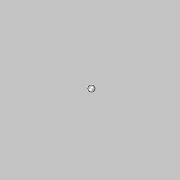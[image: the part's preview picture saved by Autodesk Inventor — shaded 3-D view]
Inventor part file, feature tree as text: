
AUTODESK INVENTOR PART (.ipt)
format: ipt  version: 2017 (Build 210142000, 142)  size: 128,000 bytes
history: native  units: mm
features: other x7, extrude x7, sketch x6, fillet x3, projected_geometry x2, plane x1
ambient origin geometry x7: Origin, YZ Plane, XZ Plane, X Axis, Y Axis, Z Axis, Center Point
bodies: Solid1 (feature_tree), Solid2 (feature_tree)
feature tree (26):
  other  "Table"
  other  "StreetLight4000"
  other  "StreetLight5000"
  other  "StreetLight6000"
  other  "FirstSketch"
  extrude  "Extrusion1"  Depth=150.0mm TaperAngle=0.0deg
  extrude  "Extrusion2"  Depth=200.0mm
  extrude  "Extrusion3"  TaperAngle=0.0deg  [1 undecoded]
  extrude  "Extrusion4"  Depth=2750.0mm TaperAngle=0.0deg
  plane  "Work Plane1"
  sketch  "Sketch8"  dims[d11=15.0deg d12=250.0mm]
  extrude  "Extrusion5"  Depth=250.0mm
  extrude  "Extrusion6"  Depth=200.0mm
  fillet  "Fillet1"  Radius=100.0mm
  fillet  "Fillet2"  Radius=75.0mm
  extrude  "Extrusion7"  Depth=100.0mm TaperAngle=0.0deg
  fillet  "Fillet3"  Radius=150.0mm
  other  "XY Ground Plane"
  sketch  "Sketch4"  dims[d0=400.0mm d1=150.0mm d2=0.0mm]
  sketch  "Sketch5"  dims[d3=100.0mm d4=-7.853982mm d5=200.0mm]
  projected_geometry  "Projected Loop1"
  sketch  "Sketch6"  dims[d6=1250.0mm d7=0.0mm]
  sketch  "Sketch7"  dims[d8=120.0mm d9=2750.0mm d10=0.0mm]
  other  "Work Axis1"
  sketch  "Sketch9"  dims[d13=200.0mm d14=200.0mm d15=100.0mm d16=75.0mm d17=100.0mm d18=0.0mm d19=150.0mm d20=0.0mm d21=40.0mm d22=50.0mm d23=5.0mm d24=60.0mm d25=0.0mm d26=50.0mm d27=0.0mm]
  projected_geometry  "Projected Loop2"
note: 1 required parameter value undecoded (feature->parameter linkage not recoverable at this tier; creation-order binding heuristic only, values carry confidence <= 0.55)
